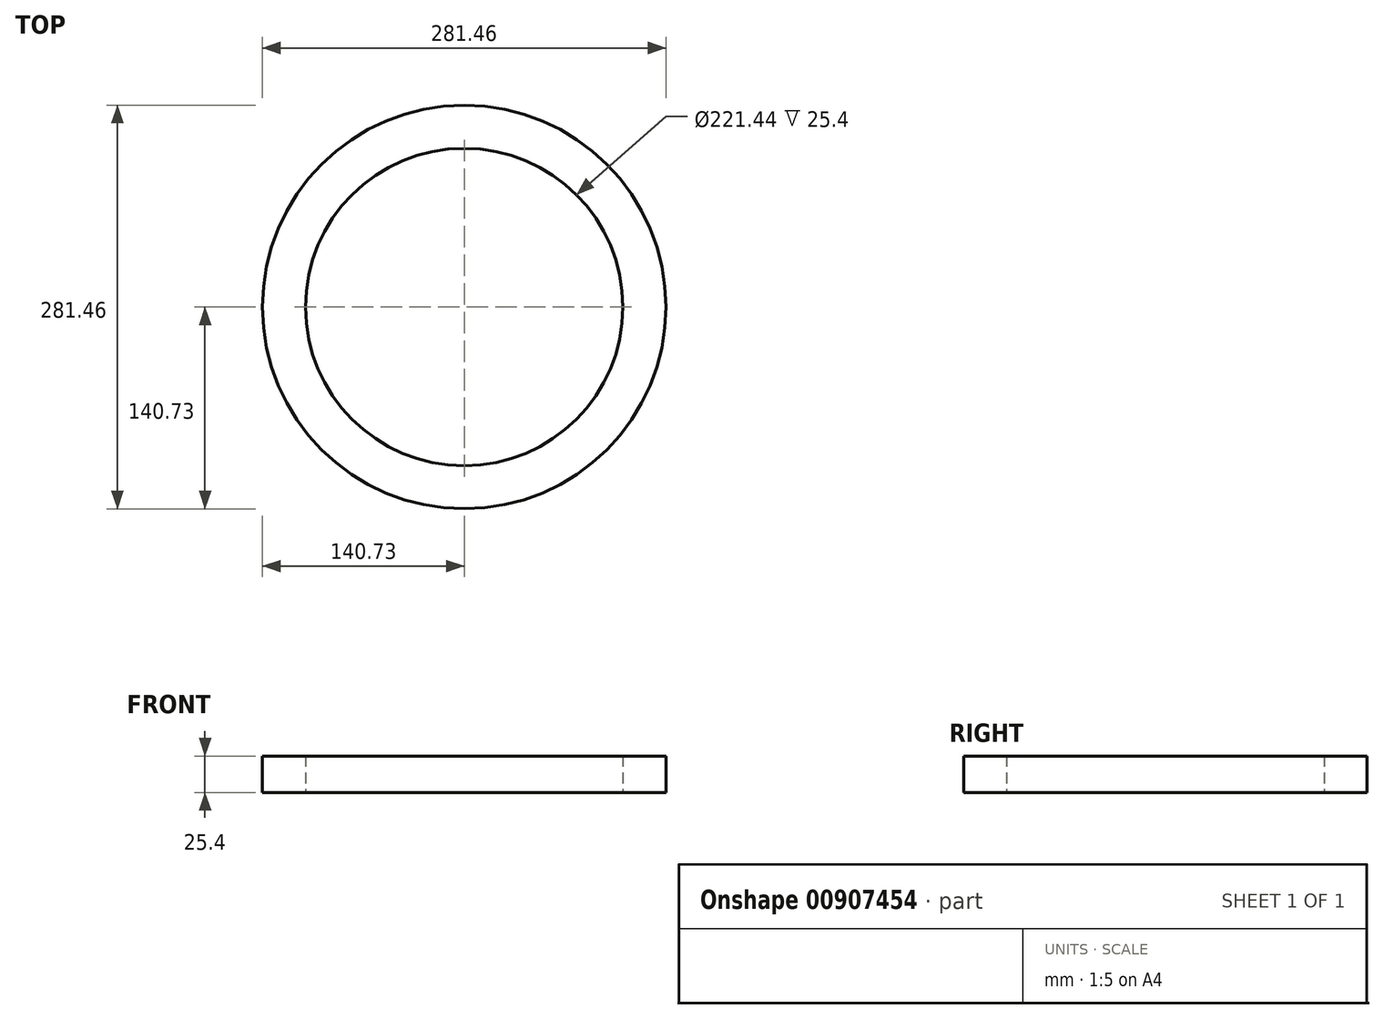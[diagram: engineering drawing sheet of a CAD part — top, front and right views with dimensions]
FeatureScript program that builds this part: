
annotation { "Feature Type Name" : "Feature", "Feature Type Description" : "" }
export const myFeature = defineFeature(function(context is Context, id is Id, definition is map)
    precondition{}
    {
        {
            var Q0;
            Q0=qCreatedBy(makeId("Top.planeOp"),FACE);
            var sketch = newSketch(context, id + "F0", { "sketchPlane" : qUnion([Q0])});
            skCircle(sketch, "E0", {"center": v(0, 0) * mm, "radius": 140.73 * mm});
            skCircle(sketch, "E1", {"center": v(0, 0) * mm, "radius": 110.72 * mm});
            skSolve(sketch);
        }
        {
            var Q0;
            Q0 = qSketchRegion(id + "F0", true);
            extrude(context, id + "F1", {"entities" : qUnion([Q0]), "depth" : 25.4 * mm, "offsetDistance" : 25.4 * mm});
        }
    });
